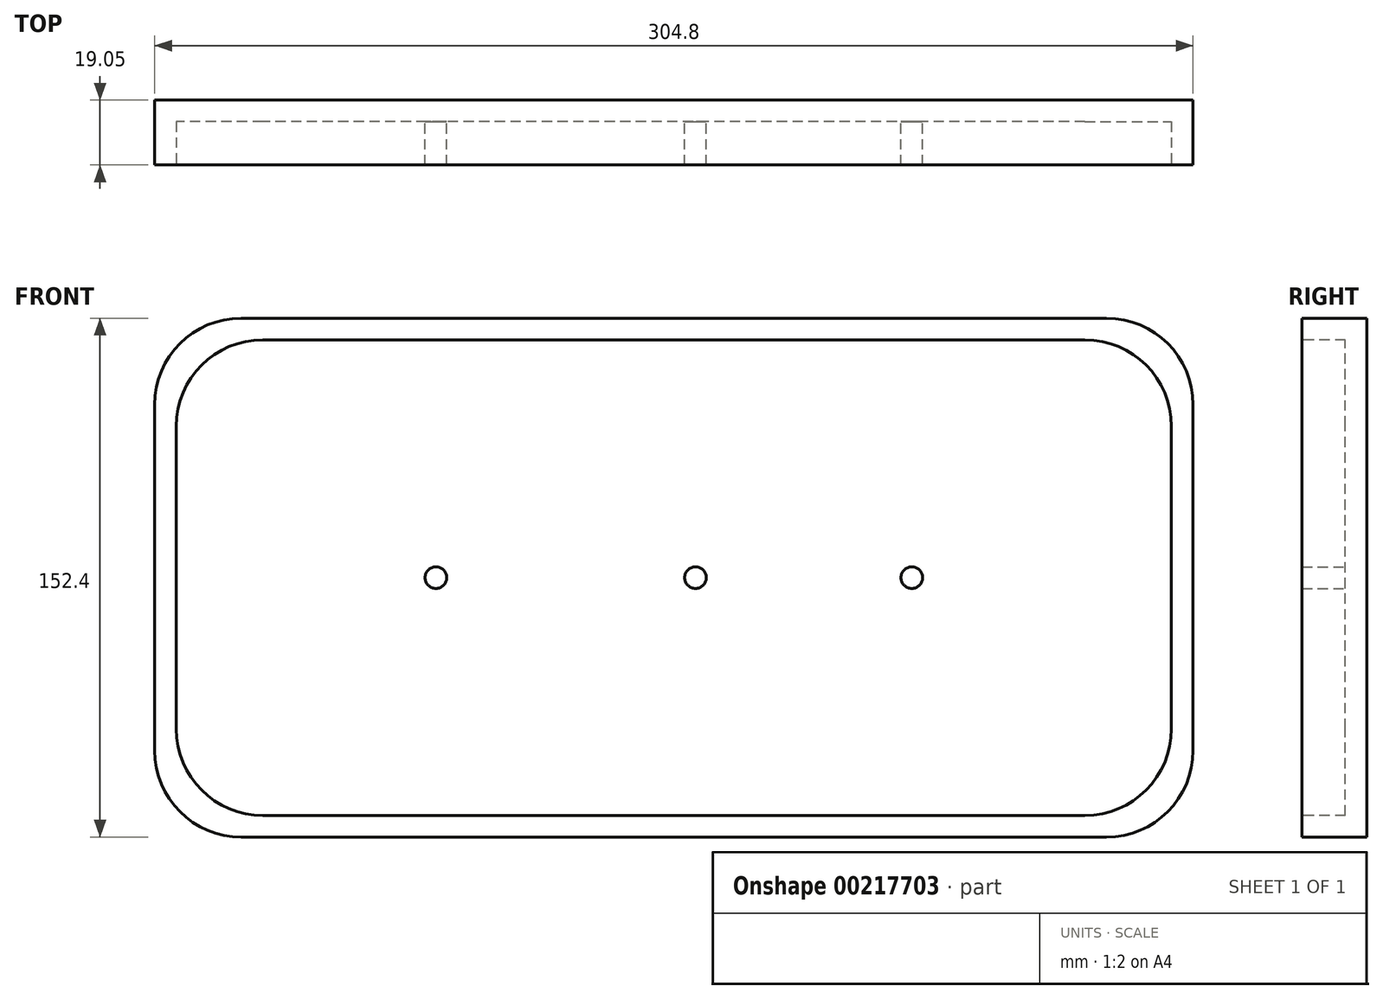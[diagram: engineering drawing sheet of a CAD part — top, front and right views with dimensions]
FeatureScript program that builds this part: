
annotation { "Feature Type Name" : "Feature", "Feature Type Description" : "" }
export const myFeature = defineFeature(function(context is Context, id is Id, definition is map)
    precondition{}
    {
        {
            var Q0;
            Q0=qCreatedBy(makeId("Front.planeOp"),FACE);
            var sketch = newSketch(context, id + "F0", { "sketchPlane" : qUnion([Q0])});
            skLineSegment(sketch, "E0", {"start": v(0, 25.4) * mm, "end": v(0, 127) * mm});
            skLineSegment(sketch, "E1", {"start": v(25.4, 152.4) * mm, "end": v(279.4, 152.4) * mm});
            skLineSegment(sketch, "E2", {"start": v(304.8, 127) * mm, "end": v(304.8, 25.4) * mm});
            skLineSegment(sketch, "E3", {"start": v(279.4, 0) * mm, "end": v(25.4, 0) * mm});
            skPoint(sketch, "E4.visualSharp", {"position": v(0, 152.4) * mm});
            skArc(sketch, "E4.filletArc", {"start": v(25.4, 152.4) * mm, "mid": v(7.44, 144.96) * mm, "end": v(0, 127) * mm});
            skPoint(sketch, "E5.visualSharp", {"position": v(0, 0) * mm});
            skArc(sketch, "E5.filletArc", {"start": v(0, 25.4) * mm, "mid": v(7.44, 7.44) * mm, "end": v(25.4, 0) * mm});
            skPoint(sketch, "E6.visualSharp", {"position": v(304.8, 0) * mm});
            skArc(sketch, "E6.filletArc", {"start": v(279.4, 0) * mm, "mid": v(297.36, 7.44) * mm, "end": v(304.8, 25.4) * mm});
            skPoint(sketch, "E7.visualSharp", {"position": v(304.8, 152.4) * mm});
            skArc(sketch, "E7.filletArc", {"start": v(304.8, 127) * mm, "mid": v(297.36, 144.96) * mm, "end": v(279.4, 152.4) * mm});
            skSolve(sketch);
        }
        {
            var Q0;
            Q0=makeQuery(id+"F0.imprint","IMPRINT",FACE,{"disambiguationData":[TD([[makeQuery(id+"F0.imprint","IMPRINT",EDGE,{"derivedFrom":sQuery(id+"F0.wireOp",EDGE,"E0")}),-1.0]])]});
            extrude(context, id + "F1", {"entities" : qUnion([Q0]), "depth" : 19.05 * mm});
        }
        {
            var Q0;
            Q0=makeQuery(id+"F1.opExtrude","CAP_FACE",FACE,{"disambiguationData":[OSD([sQuery(id+"F0.wireOp",EDGE,"E0"),sQuery(id+"F0.wireOp",EDGE,"E1"),sQuery(id+"F0.wireOp",EDGE,"E2"),sQuery(id+"F0.wireOp",EDGE,"E3"),sQuery(id+"F0.wireOp",EDGE,"E4.filletArc"),sQuery(id+"F0.wireOp",EDGE,"E5.filletArc"),sQuery(id+"F0.wireOp",EDGE,"E6.filletArc"),sQuery(id+"F0.wireOp",EDGE,"E7.filletArc")])],"isStart":false});
            var sketch = newSketch(context, id + "F2", { "sketchPlane" : qUnion([Q0])});
            skPoint(sketch, "E8", {"position": v(0, 61.62) * mm});
            skPoint(sketch, "E9", {"position": v(78.83, 0) * mm});
            skPoint(sketch, "E10", {"position": v(78.83, 6.35) * mm});
            skLineSegment(sketch, "E11", {"start": v(152.4, 163.97) * mm, "end": v(152.4, -24.93) * mm, "construction": true});
            skLineSegment(sketch, "E12", {"start": v(6.35, 31.75) * mm, "end": v(6.35, 76.2) * mm});
            skLineSegment(sketch, "E13", {"start": v(31.75, 6.35) * mm, "end": v(152.4, 6.35) * mm});
            skPoint(sketch, "E14.visualSharp", {"position": v(6.35, 6.35) * mm});
            skArc(sketch, "E14.filletArc", {"start": v(6.35, 31.75) * mm, "mid": v(13.79, 13.79) * mm, "end": v(31.75, 6.35) * mm});
            skLineSegment(sketch, "E15.MirrorCS", {"start": v(6.35, 120.65) * mm, "end": v(6.35, 76.2) * mm});
            skArc(sketch, "E16.MirrorCS", {"start": v(6.35, 120.65) * mm, "mid": v(13.79, 138.61) * mm, "end": v(31.75, 146.05) * mm});
            skLineSegment(sketch, "E17.MirrorCS", {"start": v(31.75, 146.05) * mm, "end": v(152.4, 146.05) * mm});
            skPoint(sketch, "E18.MirrorP", {"position": v(225.97, 0) * mm});
            skLineSegment(sketch, "E19.MirrorCS", {"start": v(273.05, 146.05) * mm, "end": v(152.4, 146.05) * mm});
            skArc(sketch, "E20.MirrorCS", {"start": v(298.45, 31.75) * mm, "mid": v(291.01, 13.79) * mm, "end": v(273.05, 6.35) * mm});
            skLineSegment(sketch, "E21.MirrorCS", {"start": v(298.45, 120.65) * mm, "end": v(298.45, 76.2) * mm});
            skPoint(sketch, "E22.MirrorP", {"position": v(304.8, 61.62) * mm});
            skPoint(sketch, "E23.MirrorP", {"position": v(298.45, 6.35) * mm});
            skLineSegment(sketch, "E24.MirrorCS", {"start": v(273.05, 6.35) * mm, "end": v(152.4, 6.35) * mm});
            skPoint(sketch, "E25.MirrorP", {"position": v(225.97, 6.35) * mm});
            skLineSegment(sketch, "E26.MirrorCS", {"start": v(298.45, 31.75) * mm, "end": v(298.45, 76.2) * mm});
            skArc(sketch, "E27.MirrorCS", {"start": v(298.45, 120.65) * mm, "mid": v(291.01, 138.61) * mm, "end": v(273.05, 146.05) * mm});
            skSolve(sketch);
        }
        {
            var Q0;
            Q0=makeQuery(id+"F2.imprint","IMPRINT",FACE,{"disambiguationData":[TD([[makeQuery(id+"F2.imprint","IMPRINT",EDGE,{"derivedFrom":sQuery(id+"F2.wireOp",EDGE,"E12")}),-1.0]])]});
            extrude(context, id + "F3", {"entities" : qUnion([Q0]), "operationType" : NewBodyOperationType.REMOVE, "oppositeDirection" : true, "depth" : 12.7 * mm});
        }
        {
            var Q0;
            Q0=makeQuery(id+"F3.boolean.opBoolean","COPY",FACE,{"derivedFrom":makeQuery(id+"F3.opExtrude","CAP_FACE",FACE,{"disambiguationData":[OSD([sQuery(id+"F2.wireOp",EDGE,"E12"),sQuery(id+"F2.wireOp",EDGE,"E13"),sQuery(id+"F2.wireOp",EDGE,"E14.filletArc"),sQuery(id+"F2.wireOp",EDGE,"E15.MirrorCS"),sQuery(id+"F2.wireOp",EDGE,"E16.MirrorCS"),sQuery(id+"F2.wireOp",EDGE,"E17.MirrorCS"),sQuery(id+"F2.wireOp",EDGE,"E19.MirrorCS"),sQuery(id+"F2.wireOp",EDGE,"E20.MirrorCS"),sQuery(id+"F2.wireOp",EDGE,"E21.MirrorCS"),sQuery(id+"F2.wireOp",EDGE,"E24.MirrorCS"),sQuery(id+"F2.wireOp",EDGE,"E26.MirrorCS"),sQuery(id+"F2.wireOp",EDGE,"E27.MirrorCS")])],"isStart":false})});
            var sketch = newSketch(context, id + "F4", { "sketchPlane" : qUnion([Q0])});
            skPoint(sketch, "E28", {"position": v(82.55, 76.2) * mm});
            skPoint(sketch, "E29", {"position": v(158.75, 76.2) * mm});
            skPoint(sketch, "E30", {"position": v(222.25, 76.2) * mm});
            skCircle(sketch, "E31", {"center": v(82.55, 76.2) * mm, "radius": 3.18 * mm});
            skCircle(sketch, "E32", {"center": v(158.75, 76.2) * mm, "radius": 3.18 * mm});
            skCircle(sketch, "E33", {"center": v(222.25, 76.2) * mm, "radius": 3.18 * mm});
            skSolve(sketch);
        }
        {
            var Q0;
            Q0 = qSketchRegion(id + "F4", true);
            extrude(context, id + "F5", {"entities" : qUnion([Q0]), "operationType" : NewBodyOperationType.ADD, "depth" : 12.7 * mm});
        }
    });
